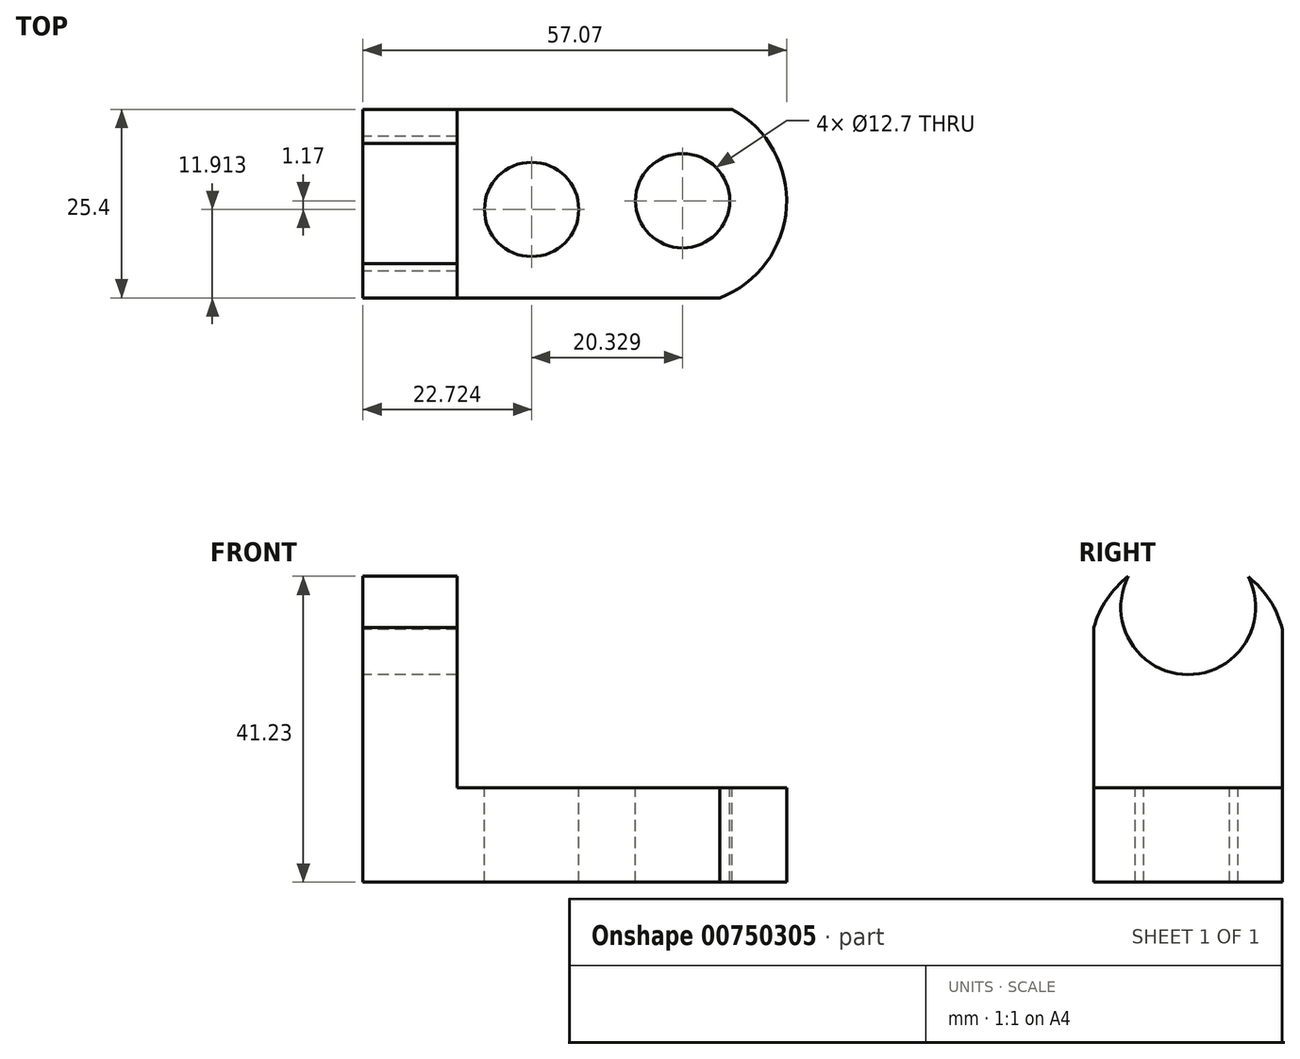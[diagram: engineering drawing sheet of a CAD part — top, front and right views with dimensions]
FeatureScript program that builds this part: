
annotation { "Feature Type Name" : "Feature", "Feature Type Description" : "" }
export const myFeature = defineFeature(function(context is Context, id is Id, definition is map)
    precondition{}
    {
        {
            var Q0;
            Q0=qCreatedBy(makeId("Front.planeOp"),FACE);
            var sketch = newSketch(context, id + "F0", { "sketchPlane" : qUnion([Q0])});
            skLineSegment(sketch, "E0", {"start": v(0, 0) * mm, "end": v(57.15, 0) * mm});
            skLineSegment(sketch, "E1", {"start": v(57.15, 44.45) * mm, "end": v(57.15, 0) * mm});
            skLineSegment(sketch, "E2", {"start": v(57.15, 44.45) * mm, "end": v(0, 44.45) * mm});
            skLineSegment(sketch, "E3", {"start": v(0, 44.45) * mm, "end": v(0, 0) * mm});
            skSolve(sketch);
        }
        {
            var Q0;
            Q0=makeQuery(id+"F0.imprint","IMPRINT",FACE,{"disambiguationData":[TD([[makeQuery(id+"F0.imprint","IMPRINT",EDGE,{"derivedFrom":sQuery(id+"F0.wireOp",EDGE,"E0")}),1.0]])]});
            var sketch = newSketch(context, id + "F1", { "sketchPlane" : qUnion([Q0])});
            skSolve(sketch);
        }
        {
            var Q0;
            Q0 = qSketchRegion(id + "F1", true);
            var Q1;
            Q1=makeQuery(id+"F0.imprint","IMPRINT",FACE,{"disambiguationData":[TD([[makeQuery(id+"F0.imprint","IMPRINT",EDGE,{"derivedFrom":sQuery(id+"F0.wireOp",EDGE,"E0")}),1.0]])]});
            extrude(context, id + "F2", {"entities" : qUnion([Q0, Q1]), "depth" : 25.4 * mm, "offsetDistance" : 25.4 * mm});
        }
        {
            var Q0;
            Q0=makeQuery(id+"F2.opExtrude","CAP_FACE",FACE,{"disambiguationData":[OSD([sQuery(id+"F0.wireOp",EDGE,"E0"),sQuery(id+"F0.wireOp",EDGE,"E1"),sQuery(id+"F0.wireOp",EDGE,"E2"),sQuery(id+"F0.wireOp",EDGE,"E3")])],"isStart":false});
            var sketch = newSketch(context, id + "F3", { "sketchPlane" : qUnion([Q0])});
            skLineSegment(sketch, "E4", {"start": v(12.7, 44.45) * mm, "end": v(12.7, 12.7) * mm});
            skLineSegment(sketch, "E5", {"start": v(12.7, 12.7) * mm, "end": v(57.15, 12.7) * mm});
            skSolve(sketch);
        }
        {
            var Q0;
            Q0 = qSketchRegion(id + "F3", true);
            var Q1;
            {var subQ0=sQuery(id+"F3.wireOp",EDGE,"E4");Q1=makeQuery(id+"F3.imprint","IMPRINT",FACE,{"disambiguationData":[TD([[makeQuery(id+"F3.imprint","IMPRINT",EDGE,{"derivedFrom":subQ0}),1.0]])]});}
            extrude(context, id + "F4", {"entities" : qUnion([Q0, Q1]), "operationType" : NewBodyOperationType.REMOVE, "oppositeDirection" : true, "depth" : 25.4 * mm, "offsetDistance" : 25.4 * mm});
        }
        {
            var Q0;
            Q0=makeQuery(id+"F2.opExtrude","SWEPT_FACE",FACE,{"disambiguationData":[OSD([sQuery(id+"F0.wireOp",EDGE,"E3")])]});
            var sketch = newSketch(context, id + "F5", { "sketchPlane" : qUnion([Q0])});
            skArc(sketch, "E6", {"start": v(25.4, 27.32) * mm, "mid": v(12.87, 43.96) * mm, "end": v(0, 27.59) * mm});
            skSolve(sketch);
        }
        {
            var Q0;
            Q0 = qSketchRegion(id + "F5", true);
            var Q1;
            {var subQ1=sQuery(id+"F0.wireOp",EDGE,"E3");var subQ6=makeQuery(id+"F2.opExtrude","SWEPT_EDGE",EDGE,{"disambiguationData":[OSD([sQuery(id+"F0.wireOp",EDGE,"E2"),subQ1])]});Q1=makeQuery(id+"F5.imprint","IMPRINT",FACE,{"disambiguationData":[TD([[makeQuery(id+"F5.imprint","IMPRINT",EDGE,{"derivedFrom":subQ6}),1.0]])]});}
            extrude(context, id + "F6", {"entities" : qUnion([Q0, Q1]), "operationType" : NewBodyOperationType.REMOVE, "oppositeDirection" : true, "depth" : 25.4 * mm, "offsetDistance" : 25.4 * mm});
        }
        {
            var Q0;
            Q0=makeQuery(id+"F2.opExtrude","SWEPT_FACE",FACE,{"disambiguationData":[OSD([sQuery(id+"F0.wireOp",EDGE,"E3")])]});
            var sketch = newSketch(context, id + "F7", { "sketchPlane" : qUnion([Q0])});
            skArc(sketch, "E7", {"start": v(4.6, 41.15) * mm, "mid": v(12.75, 27.98) * mm, "end": v(20.76, 41.23) * mm});
            skSolve(sketch);
        }
        {
            var Q0;
            Q0 = qSketchRegion(id + "F7", true);
            var Q1;
            {var subQ0=sQuery(id+"F7.wireOp",EDGE,"E7");Q1=makeQuery(id+"F7.imprint","IMPRINT",FACE,{"disambiguationData":[TD([[makeQuery(id+"F7.imprint","IMPRINT",EDGE,{"derivedFrom":subQ0}),1.0]])]});}
            extrude(context, id + "F8", {"entities" : qUnion([Q0, Q1]), "operationType" : NewBodyOperationType.REMOVE, "oppositeDirection" : true, "depth" : 25.4 * mm, "offsetDistance" : 25.4 * mm});
        }
        {
            var Q0;
            Q0=makeQuery(id+"F4.boolean.opBoolean","COPY",FACE,{"derivedFrom":makeQuery(id+"F4.opExtrude","SWEPT_FACE",FACE,{"disambiguationData":[OSD([sQuery(id+"F3.wireOp",EDGE,"E5")])]})});
            var sketch = newSketch(context, id + "F9", { "sketchPlane" : qUnion([Q0])});
            skArc(sketch, "E8", {"start": v(48.07, -25.4) * mm, "mid": v(57.04, -13.23) * mm, "end": v(49.73, 0) * mm});
            skSolve(sketch);
        }
        {
            var Q0;
            Q0 = qSketchRegion(id + "F9", true);
            var Q1;
            {var subQ0=sQuery(id+"F9.wireOp",EDGE,"E8");Q1=makeQuery(id+"F9.imprint","IMPRINT",FACE,{"disambiguationData":[TD([[makeQuery(id+"F9.imprint","IMPRINT",EDGE,{"derivedFrom":subQ0}),-1.0]])]});}
            extrude(context, id + "F10", {"entities" : qUnion([Q0, Q1]), "operationType" : NewBodyOperationType.REMOVE, "oppositeDirection" : true, "depth" : 25.4 * mm, "offsetDistance" : 25.4 * mm});
        }
        {
            var Q0;
            Q0=makeQuery(id+"F4.boolean.opBoolean","COPY",FACE,{"derivedFrom":makeQuery(id+"F4.opExtrude","SWEPT_FACE",FACE,{"disambiguationData":[OSD([sQuery(id+"F3.wireOp",EDGE,"E5")])]})});
            var sketch = newSketch(context, id + "F11", { "sketchPlane" : qUnion([Q0])});
            skCircle(sketch, "E9", {"center": v(43.05, -12.32) * mm, "radius": 6.35 * mm});
            skCircle(sketch, "E10", {"center": v(22.72, -13.49) * mm, "radius": 6.35 * mm});
            skSolve(sketch);
        }
        {
            var Q0;
            Q0=makeQuery(id+"F11.imprint","IMPRINT",FACE,{"disambiguationData":[TD([[makeQuery(id+"F11.imprint","IMPRINT",EDGE,{"derivedFrom":sQuery(id+"F11.wireOp",EDGE,"E10")}),1.0]])]});
            var Q1;
            Q1=makeQuery(id+"F11.imprint","IMPRINT",FACE,{"disambiguationData":[TD([[makeQuery(id+"F11.imprint","IMPRINT",EDGE,{"derivedFrom":sQuery(id+"F11.wireOp",EDGE,"E9")}),1.0]])]});
            extrude(context, id + "F12", {"entities" : qUnion([Q0, Q1]), "operationType" : NewBodyOperationType.REMOVE, "oppositeDirection" : true, "depth" : 25.4 * mm, "offsetDistance" : 25.4 * mm});
        }
    });
